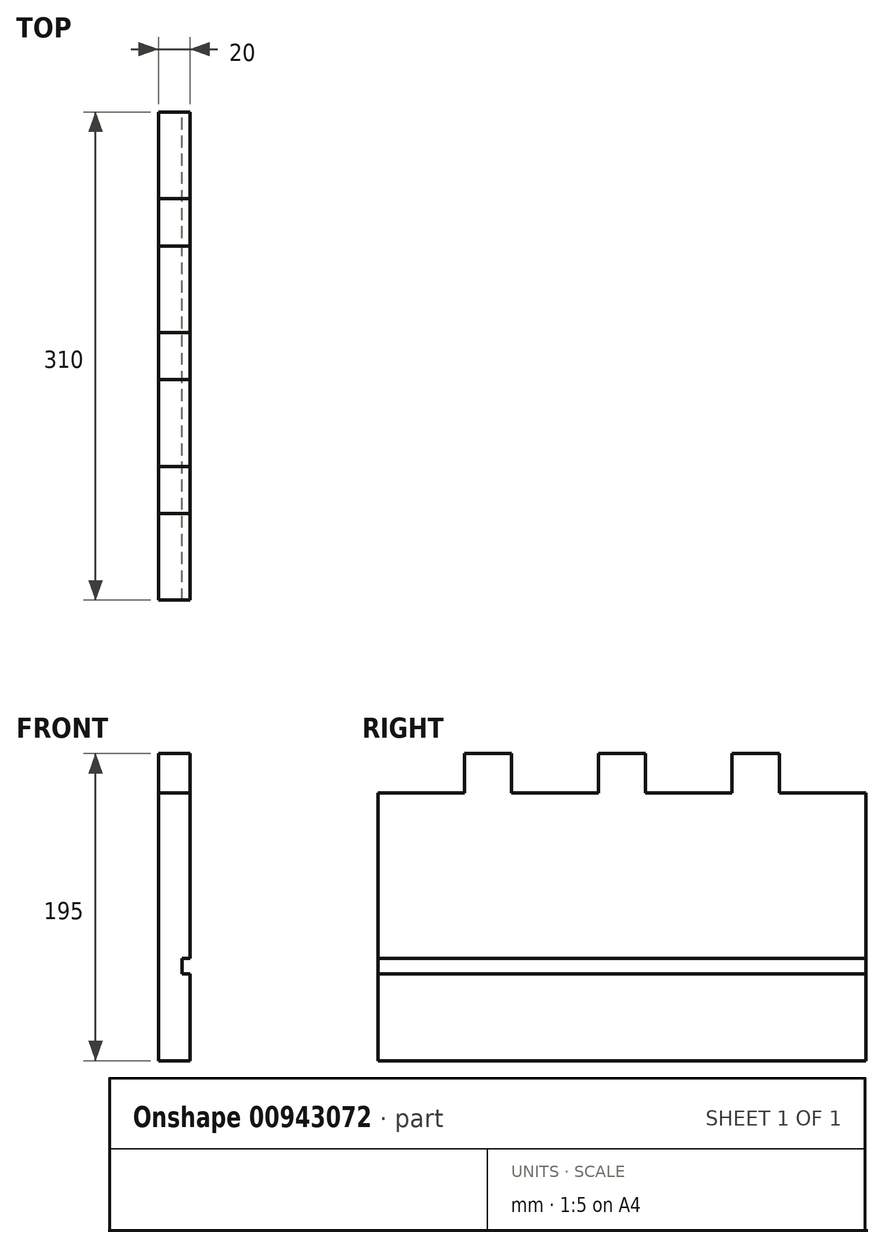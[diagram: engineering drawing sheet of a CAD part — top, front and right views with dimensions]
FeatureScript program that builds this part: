
annotation { "Feature Type Name" : "Feature", "Feature Type Description" : "" }
export const myFeature = defineFeature(function(context is Context, id is Id, definition is map)
    precondition{}
    {
        {
            var Q0;
            Q0=qCreatedBy(makeId("Right.planeOp"),FACE);
            var sketch = newSketch(context, id + "F0", { "sketchPlane" : qUnion([Q0])});
            skLineSegment(sketch, "E0.bottom", {"start": v(-191.91, 16.05) * mm, "end": v(118.09, 16.05) * mm});
            skLineSegment(sketch, "E0.top", {"start": v(-191.91, -153.95) * mm, "end": v(118.09, -153.95) * mm});
            skLineSegment(sketch, "E0.left", {"start": v(-191.91, 16.05) * mm, "end": v(-191.91, -153.95) * mm});
            skLineSegment(sketch, "E0.right", {"start": v(118.09, 16.05) * mm, "end": v(118.09, -153.95) * mm});
            skLineSegment(sketch, "E1.bottom", {"start": v(-136.91, 16.05) * mm, "end": v(-106.91, 16.05) * mm});
            skLineSegment(sketch, "E1.top", {"start": v(-136.91, 41.05) * mm, "end": v(-106.91, 41.05) * mm});
            skLineSegment(sketch, "E1.left", {"start": v(-136.91, 16.05) * mm, "end": v(-136.91, 41.05) * mm});
            skLineSegment(sketch, "E1.right", {"start": v(-106.91, 16.05) * mm, "end": v(-106.91, 41.05) * mm});
            skLineSegment(sketch, "E2.bottom", {"start": v(-51.91, 16.05) * mm, "end": v(-21.91, 16.05) * mm});
            skLineSegment(sketch, "E2.top", {"start": v(-51.91, 41.05) * mm, "end": v(-21.91, 41.05) * mm});
            skLineSegment(sketch, "E2.left", {"start": v(-51.91, 16.05) * mm, "end": v(-51.91, 41.05) * mm});
            skLineSegment(sketch, "E2.right", {"start": v(-21.91, 16.05) * mm, "end": v(-21.91, 41.05) * mm});
            skLineSegment(sketch, "E3.bottom", {"start": v(33.09, 16.05) * mm, "end": v(63.09, 16.05) * mm});
            skLineSegment(sketch, "E3.top", {"start": v(33.09, 41.05) * mm, "end": v(63.09, 41.05) * mm});
            skLineSegment(sketch, "E3.left", {"start": v(33.09, 16.05) * mm, "end": v(33.09, 41.05) * mm});
            skLineSegment(sketch, "E3.right", {"start": v(63.09, 16.05) * mm, "end": v(63.09, 41.05) * mm});
            skSolve(sketch);
        }
        {
            var Q0;
            Q0 = qSketchRegion(id + "F0", true);
            extrude(context, id + "F1", {"entities" : qUnion([Q0]), "depth" : 20 * mm, "offsetDistance" : 25 * mm});
        }
        {
            var Q0;
            Q0=makeQuery(id+"F1.opExtrude","CAP_FACE",FACE,{"disambiguationData":[OSD([sQuery(id+"F0.wireOp",EDGE,"E0.bottom"),sQuery(id+"F0.wireOp",EDGE,"E0.top"),sQuery(id+"F0.wireOp",EDGE,"E0.left"),sQuery(id+"F0.wireOp",EDGE,"E0.right"),sQuery(id+"F0.wireOp",EDGE,"E1.top"),sQuery(id+"F0.wireOp",EDGE,"E1.left"),sQuery(id+"F0.wireOp",EDGE,"E1.right"),sQuery(id+"F0.wireOp",EDGE,"E2.top"),sQuery(id+"F0.wireOp",EDGE,"E2.left"),sQuery(id+"F0.wireOp",EDGE,"E2.right"),sQuery(id+"F0.wireOp",EDGE,"E3.top"),sQuery(id+"F0.wireOp",EDGE,"E3.left"),sQuery(id+"F0.wireOp",EDGE,"E3.right")])],"isStart":false});
            var sketch = newSketch(context, id + "F2", { "sketchPlane" : qUnion([Q0])});
            skLineSegment(sketch, "E4.bottom", {"start": v(-191.91, -88.95) * mm, "end": v(118.09, -88.95) * mm});
            skLineSegment(sketch, "E4.top", {"start": v(-191.91, -98.95) * mm, "end": v(118.09, -98.95) * mm});
            skLineSegment(sketch, "E4.left", {"start": v(-191.91, -88.95) * mm, "end": v(-191.91, -98.95) * mm});
            skLineSegment(sketch, "E4.right", {"start": v(118.09, -88.95) * mm, "end": v(118.09, -98.95) * mm});
            skSolve(sketch);
        }
        {
            var Q0;
            Q0=makeQuery(id+"F2.imprint","IMPRINT",FACE,{"disambiguationData":[TD([[makeQuery(id+"F2.imprint","IMPRINT",EDGE,{"derivedFrom":sQuery(id+"F2.wireOp",EDGE,"E4.bottom")}),-1.0]])]});
            extrude(context, id + "F3", {"entities" : qUnion([Q0]), "operationType" : NewBodyOperationType.REMOVE, "oppositeDirection" : true, "depth" : 5 * mm, "offsetDistance" : 25 * mm});
        }
    });
